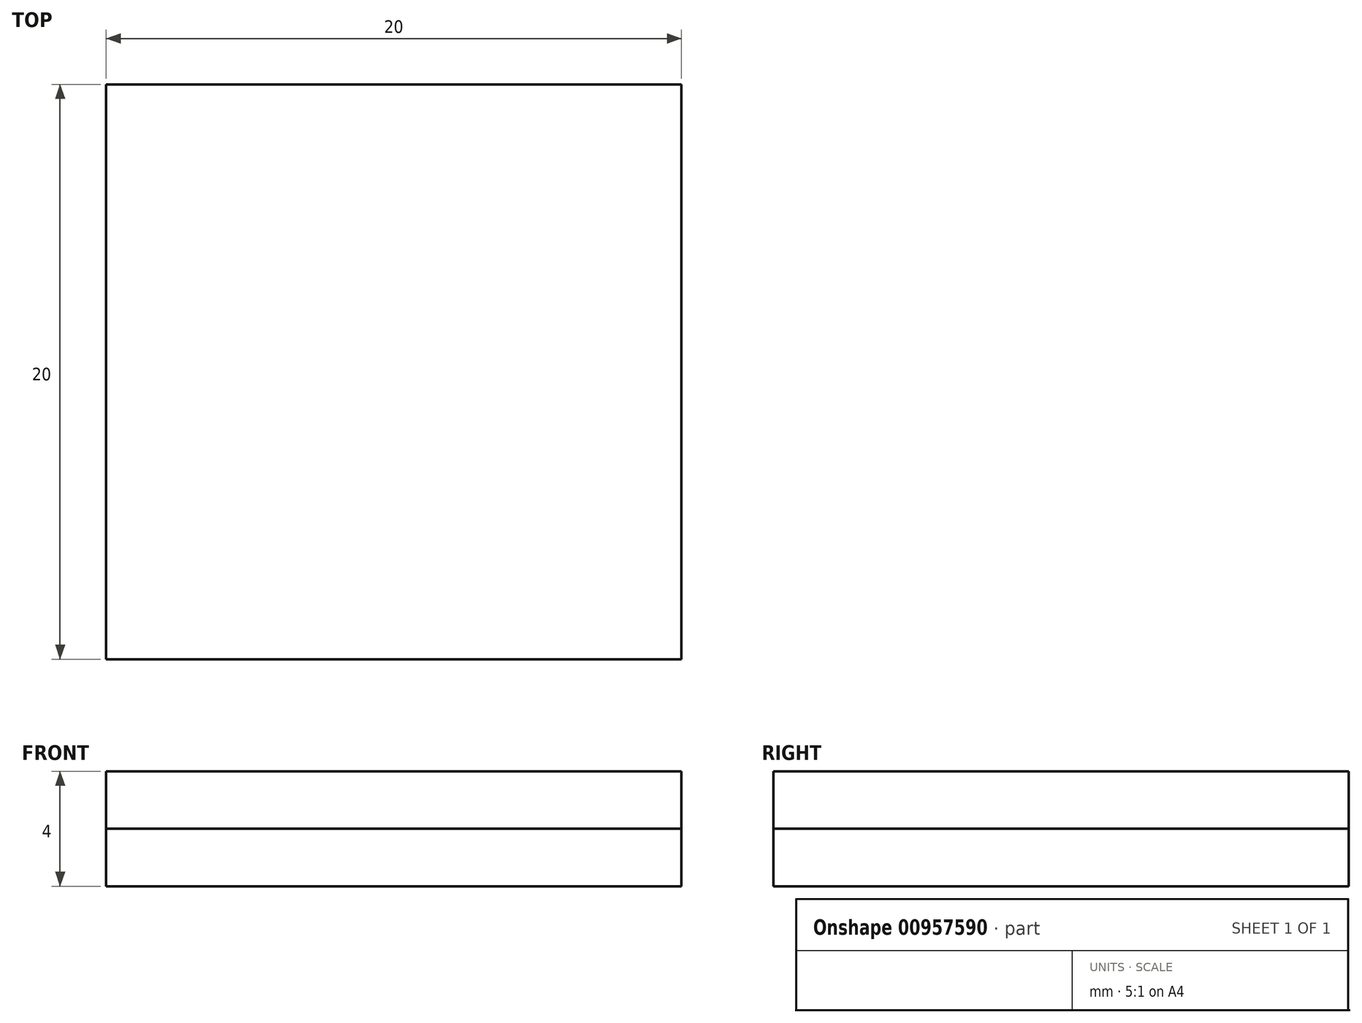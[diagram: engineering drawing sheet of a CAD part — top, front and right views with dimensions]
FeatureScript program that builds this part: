
annotation { "Feature Type Name" : "Feature", "Feature Type Description" : "" }
export const myFeature = defineFeature(function(context is Context, id is Id, definition is map)
    precondition{}
    {
        {
            var Q0;
            Q0=qCreatedBy(makeId("Top.planeOp"),FACE);
            var sketch = newSketch(context, id + "F0", { "sketchPlane" : qUnion([Q0])});
            skLineSegment(sketch, "E0.bottom", {"start": v(-10, 10) * mm, "end": v(10, 10) * mm});
            skLineSegment(sketch, "E0.top", {"start": v(-10, -10) * mm, "end": v(10, -10) * mm});
            skLineSegment(sketch, "E0.left", {"start": v(-10, 10) * mm, "end": v(-10, -10) * mm});
            skLineSegment(sketch, "E0.right", {"start": v(10, 10) * mm, "end": v(10, -10) * mm});
            skPoint(sketch, "E0.middle", {"position": v(0, 0) * mm});
            skSolve(sketch);
        }
        {
            var Q0;
            Q0 = qSketchRegion(id + "F0", true);
            extrude(context, id + "F1", {"entities" : qUnion([Q0]), "depth" : 2 * mm, "offsetDistance" : 25 * mm});
        }
        {
            var Q0;
            Q0=qCreatedBy(makeId("Top.planeOp"),FACE);
            var sketch = newSketch(context, id + "F2", { "sketchPlane" : qUnion([Q0])});
            skLineSegment(sketch, "E1.bottom", {"start": v(-10, 10) * mm, "end": v(10, 10) * mm});
            skLineSegment(sketch, "E1.top", {"start": v(-10, -10) * mm, "end": v(10, -10) * mm});
            skLineSegment(sketch, "E1.left", {"start": v(-10, 10) * mm, "end": v(-10, -10) * mm});
            skLineSegment(sketch, "E1.right", {"start": v(10, 10) * mm, "end": v(10, -10) * mm});
            skPoint(sketch, "E1.middle", {"position": v(0, 0) * mm});
            skSolve(sketch);
        }
        {
            var Q0;
            Q0 = qSketchRegion(id + "F2", true);
            extrude(context, id + "F3", {"entities" : qUnion([Q0]), "oppositeDirection" : true, "depth" : 2 * mm, "offsetDistance" : 25 * mm});
        }
        {
            var Q0;
            Q0 = qSketchRegion(id + "F2", true);
            extrude(context, id + "F4", {"entities" : qUnion([Q0]), "depth" : 2 * mm, "offsetDistance" : 25 * mm});
        }
    });
